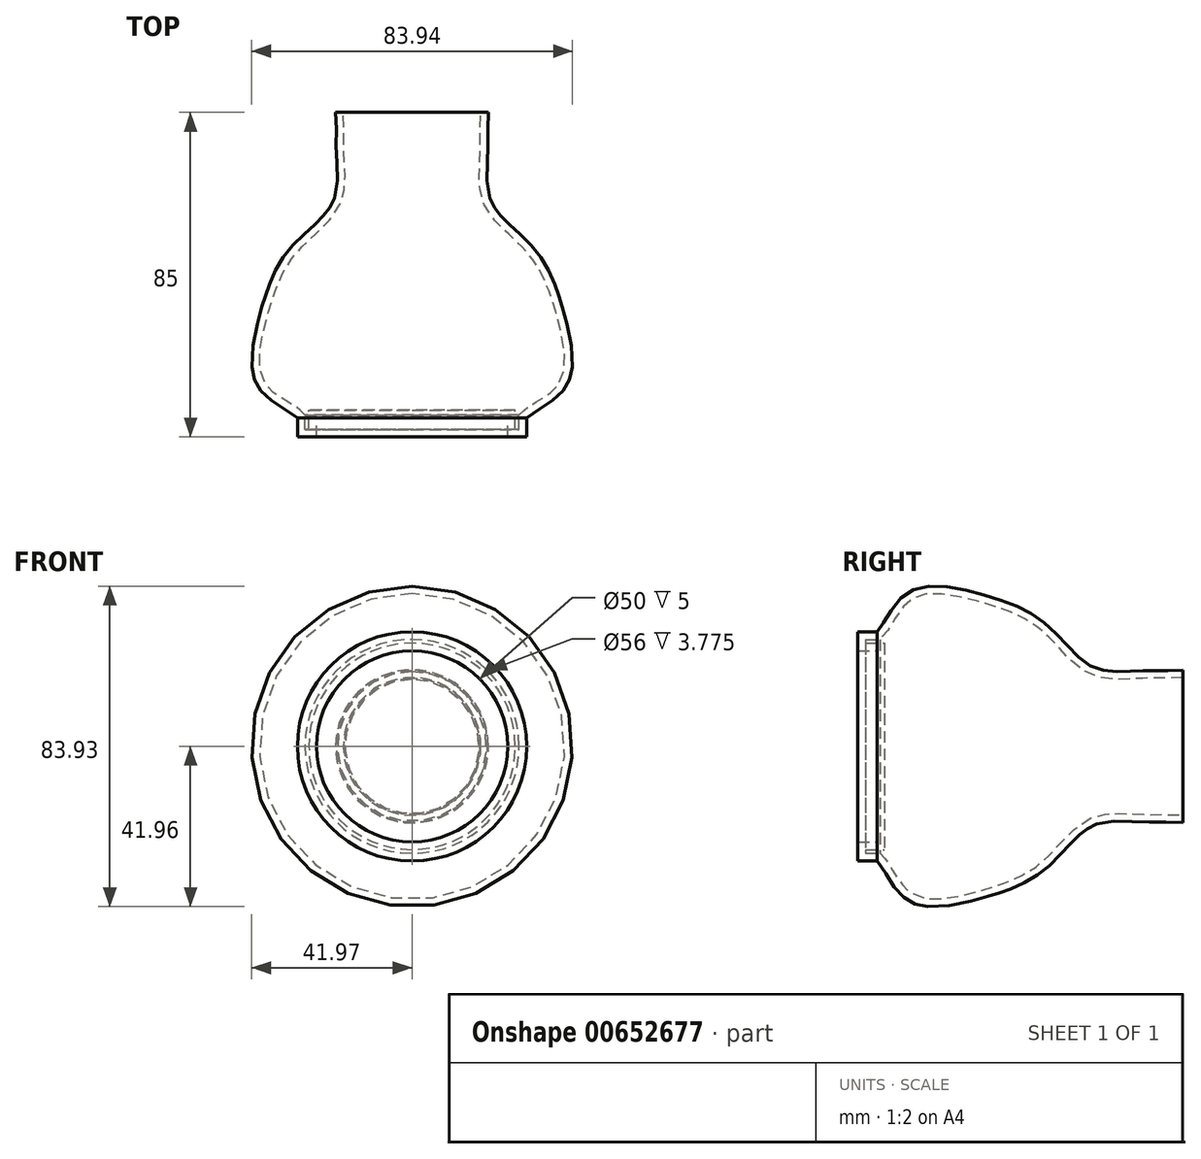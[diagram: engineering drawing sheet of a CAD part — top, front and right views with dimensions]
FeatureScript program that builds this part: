
annotation { "Feature Type Name" : "Feature", "Feature Type Description" : "" }
export const myFeature = defineFeature(function(context is Context, id is Id, definition is map)
    precondition{}
    {
        {
            var Q0;
            Q0=qCreatedBy(makeId("Top.planeOp"),FACE);
            var sketch = newSketch(context, id + "F0", { "sketchPlane" : qUnion([Q0])});
            skLineSegment(sketch, "E0", {"start": v(0, 40.71) * mm, "end": v(20, 40.71) * mm});
            skLineSegment(sketch, "E1", {"start": v(0, -39.29) * mm, "end": v(25, -39.29) * mm});
            skLineSegment(sketch, "E2", {"start": v(25, -39.29) * mm, "end": v(25, -44.29) * mm});
            skLineSegment(sketch, "E3", {"start": v(25, -44.29) * mm, "end": v(30, -44.29) * mm});
            skLineSegment(sketch, "E4", {"start": v(30, -44.29) * mm, "end": v(30, -39.29) * mm});
            skLineSegment(sketch, "E5", {"start": v(0, 40.71) * mm, "end": v(0, -39.29) * mm});
            skFitSpline(sketch, "E6", {"points": [v(20, 40.71) * mm, v(19.8, 29.29) * mm, v(20.75, 17.22) * mm, v(31.86, 5.13) * mm, v(39.6, -11.3) * mm, v(40.26, -31.26) * mm, v(30, -39.29) * mm], "startDerivative": vector(-7.01, -98.37) * mm, "endDerivative": vector(-35.79, -39.23) * mm});
            skSolve(sketch);
        }
        {
            var Q0;
            Q0=makeQuery(id+"F0.imprint","IMPRINT",FACE,{"disambiguationData":[TD([[makeQuery(id+"F0.imprint","IMPRINT",EDGE,{"derivedFrom":sQuery(id+"F0.wireOp",EDGE,"E0")}),-1.0]])]});
            var Q1;
            Q1=sQuery(id+"F0.wireOp",EDGE,"E5");
            revolve(context, id + "F1", {"surfaceOperationType" : NewSurfaceOperationType.NEW, "entities" : qUnion([Q0]), "axis" : qUnion([Q1]), "revolveType" : RevolveType.FULL});
        }
        {
            var Q0;
            Q0=makeQuery(id+"F1.opRevolve","SWEPT_FACE",FACE,{"disambiguationData":[OSD([sQuery(id+"F0.wireOp",EDGE,"E0")])]});
            shell(context, id + "F2", {"entities" : qUnion([Q0]), "thickness" : 2 * mm});
        }
    });
